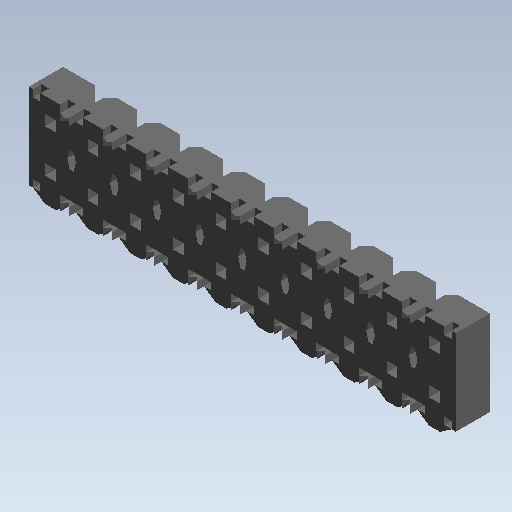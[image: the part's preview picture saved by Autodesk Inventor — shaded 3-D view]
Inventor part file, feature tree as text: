
AUTODESK INVENTOR PART (.ipt)
format: ipt  version: 2021 (Build 250183000, 183)  size: 961,536 bytes
history: native  units: mm (DEFAULTED — no unit token found)
features: extrude x10, sketch x10, other x7, thicken_offset x2, pattern_linear x1
ambient origin geometry x8: Origin, YZ Plane, XZ Plane, XY Plane, X Axis, Y Axis, Z Axis, Center Point
bodies: Solid1 (feature_tree), body_XY (feature_tree), body_YZ (feature_tree), body_ZX (feature_tree), body_X (feature_tree), body_Y (feature_tree), body_Z (feature_tree), body_Center (feature_tree)
feature tree (30):
  extrude  "Extrusion1"  Depth=2.032mm TaperAngle=0.0deg
  extrude  "Extrusion2"  Depth=50.8mm TaperAngle=0.0deg
  extrude  "Extrusion3"  Depth=10.16mm TaperAngle=0.0deg
  extrude  "Extrusion4"  Depth=10.16mm TaperAngle=0.0deg
  extrude  "Extrusion5"  Depth=5.08mm TaperAngle=0.0deg
  extrude  "Extrusion6"  Depth=2.54mm
  extrude  "Extrusion7"  Depth=1.0mm
  extrude  "Extrusion8"  [1 undecoded]
  extrude  "Extrusion9"  [1 undecoded]
  extrude  "Extrusion10"  [1 undecoded]
  pattern_linear  "Rectangular Pattern1"  [2 undecoded]
  other  "pin_XY"
  other  "pin_YZ"
  other  "pin_ZX"
  other  "pin_X"
  other  "pin_Y"
  other  "pin_Z"
  other  "pin_Center"
  thicken_offset  "Thicken1"
  thicken_offset  "Thicken2"
  sketch  "Sketch_38"
  sketch  "Sketch_35"
  sketch  "Sketch_2"  dims[d0=2.54mm d1=0.0mm d2=2.032mm d3=0.0mm]
  sketch  "Sketch_3"  dims[d4=50.8mm d5=0.0mm d6=50.8mm d7=0.0mm]
  sketch  "Sketch_6"  dims[d8=10.16mm d9=0.0mm d10=10.16mm d11=0.0mm]
  sketch  "Sketch_9"  dims[d12=50.8mm d13=0.0mm d14=10.16mm d15=0.0mm]
  sketch  "Sketch_11"  dims[d16=10.16mm d17=0.0mm d18=5.08mm d19=0.0mm]
  sketch  "Sketch_18"  dims[d27=1.0mm d28=1.0mm]
  sketch  "Sketch_20"  dims[d29=1.0mm]
  sketch  "Sketch_17"  dims[d20=90.0mm d22=2.54mm d23=10.0mm d25=0.0mm d26=1.0mm]
note: 5 required parameter values undecoded (feature->parameter linkage not recoverable at this tier; creation-order binding heuristic only, values carry confidence <= 0.55)
